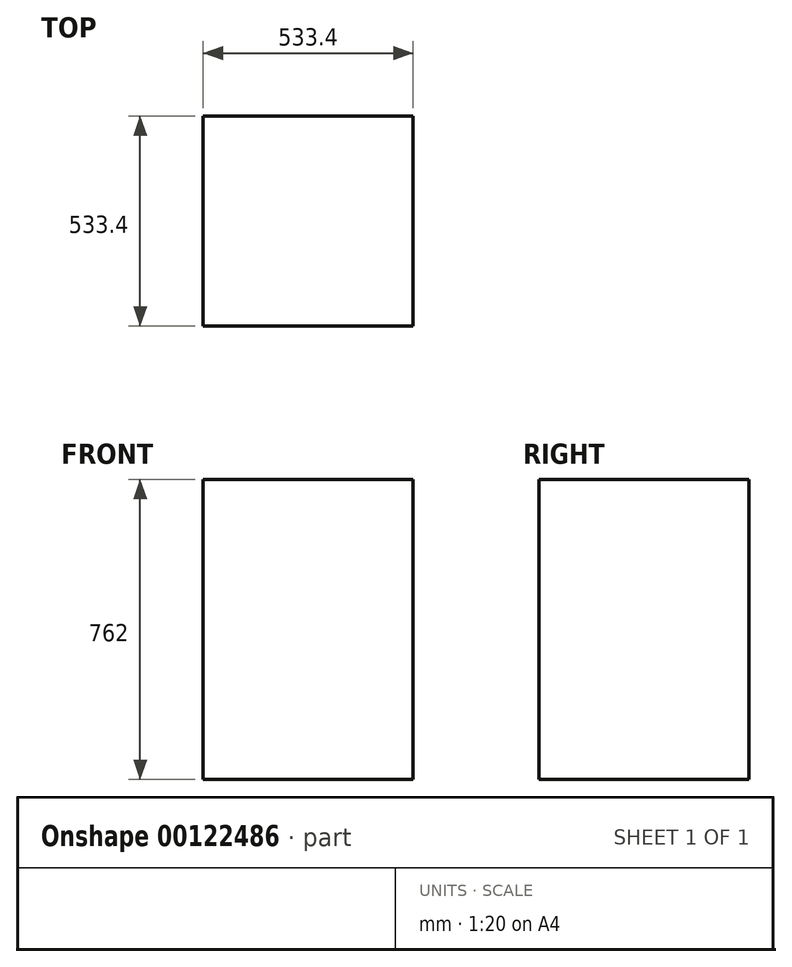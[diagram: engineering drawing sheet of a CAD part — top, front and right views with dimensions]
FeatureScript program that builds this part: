
annotation { "Feature Type Name" : "Feature", "Feature Type Description" : "" }
export const myFeature = defineFeature(function(context is Context, id is Id, definition is map)
    precondition{}
    {
        {
            var Q0;
            Q0=qCreatedBy(makeId("Top.planeOp"),FACE);
            var sketch = newSketch(context, id + "F0", { "sketchPlane" : qUnion([Q0])});
            skLineSegment(sketch, "E0.bottom", {"start": v(0, 0) * mm, "end": v(533.4, 0) * mm});
            skLineSegment(sketch, "E0.top", {"start": v(0, -533.4) * mm, "end": v(533.4, -533.4) * mm});
            skLineSegment(sketch, "E0.left", {"start": v(0, 0) * mm, "end": v(0, -533.4) * mm});
            skLineSegment(sketch, "E0.right", {"start": v(533.4, 0) * mm, "end": v(533.4, -533.4) * mm});
            skSolve(sketch);
        }
        {
            var Q0;
            Q0 = qSketchRegion(id + "F0", true);
            extrude(context, id + "F1", {"entities" : qUnion([Q0]), "depth" : 762 * mm});
        }
    });
